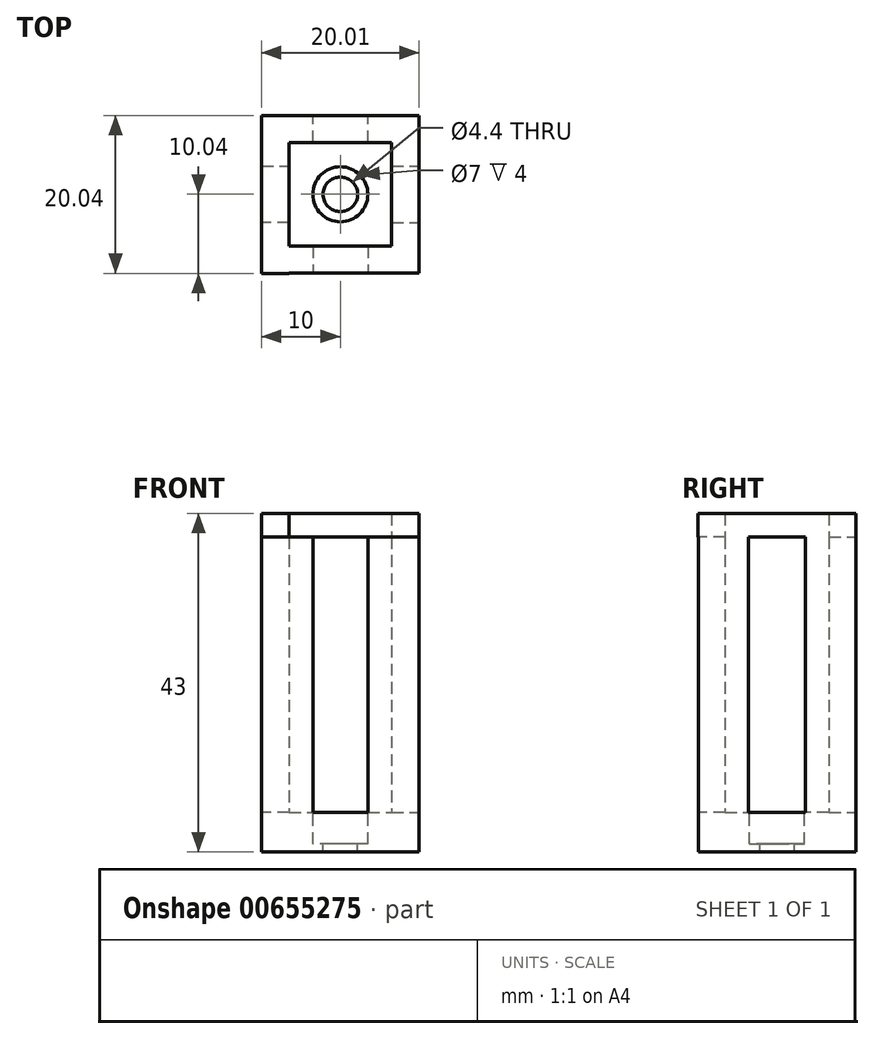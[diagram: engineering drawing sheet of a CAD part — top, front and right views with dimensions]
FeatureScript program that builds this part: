
annotation { "Feature Type Name" : "Feature", "Feature Type Description" : "" }
export const myFeature = defineFeature(function(context is Context, id is Id, definition is map)
    precondition{}
    {
        {
            var Q0;
            Q0=qCreatedBy(makeId("Top.planeOp"),FACE);
            var sketch = newSketch(context, id + "F0", { "sketchPlane" : qUnion([Q0])});
            skLineSegment(sketch, "E0.bottom", {"start": v(10, -10) * mm, "end": v(-10, -10) * mm});
            skLineSegment(sketch, "E0.top", {"start": v(10, 10) * mm, "end": v(-10, 10) * mm});
            skLineSegment(sketch, "E0.left", {"start": v(10, -10) * mm, "end": v(10, 10) * mm});
            skLineSegment(sketch, "E0.right", {"start": v(-10, -10) * mm, "end": v(-10, 10) * mm});
            skPoint(sketch, "E0.middle", {"position": v(0, 0) * mm});
            skSolve(sketch);
        }
        {
            var Q0;
            Q0=makeQuery(id+"F0.imprint","IMPRINT",FACE,{"disambiguationData":[TD([[makeQuery(id+"F0.imprint","IMPRINT",EDGE,{"derivedFrom":sQuery(id+"F0.wireOp",EDGE,"E0.bottom")}),-1.0]])]});
            extrude(context, id + "F1", {"entities" : qUnion([Q0]), "depth" : 5 * mm});
        }
        {
            var Q0;
            Q0=makeQuery(id+"F1.opExtrude","CAP_FACE",FACE,{"disambiguationData":[OSD([sQuery(id+"F0.wireOp",EDGE,"E0.bottom"),sQuery(id+"F0.wireOp",EDGE,"E0.top"),sQuery(id+"F0.wireOp",EDGE,"E0.left"),sQuery(id+"F0.wireOp",EDGE,"E0.right")])],"isStart":false});
            var sketch = newSketch(context, id + "F2", { "sketchPlane" : qUnion([Q0])});
            skPoint(sketch, "E1", {"position": v(0, 0) * mm});
            skSolve(sketch);
        }
        {
            var Q0;
            Q0=sQuery(id+"F2.wireOp",VERTEX,"E1");
            var Q1;
            Q1=makeQuery(id+"F1.opExtrude","SWEPT_BODY",BODY,{"disambiguationData":[OSD([sQuery(id+"F0.wireOp",EDGE,"E0.bottom"),sQuery(id+"F0.wireOp",EDGE,"E0.top"),sQuery(id+"F0.wireOp",EDGE,"E0.left"),sQuery(id+"F0.wireOp",EDGE,"E0.right")])]});
            hole(context, id + "F3", {"style" : HoleStyle.SIMPLE, "endStyle" : HoleEndStyle.THROUGH, "standardTappedOrClearance" : lookupTablePath({ "standard" : "ISO", "fit" : "Normal", "size" : "M4", "type" : "Clearance" }), "standardBlindInLast" : lookupTablePath({ "fit" : "Standard", "standard" : "ISO", "size" : "M4", "type" : "Clearance" }), "holeDiameter" : 4.4 * mm, "tappedDepth" : 12 * mm, "tapClearance" : 3, "locations" : qUnion([Q0]), "scope" : qUnion([Q1])});
        }
        {
            var Q0;
            Q0=makeQuery(id+"F1.opExtrude","CAP_FACE",FACE,{"disambiguationData":[OSD([sQuery(id+"F0.wireOp",EDGE,"E0.bottom"),sQuery(id+"F0.wireOp",EDGE,"E0.top"),sQuery(id+"F0.wireOp",EDGE,"E0.left"),sQuery(id+"F0.wireOp",EDGE,"E0.right")])],"isStart":false});
            var sketch = newSketch(context, id + "F4", { "sketchPlane" : qUnion([Q0])});
            skPoint(sketch, "E2.middle", {"position": v(0, 0) * mm});
            skLineSegment(sketch, "E3.bottom", {"start": v(-6.5, 6.6) * mm, "end": v(-10, 6.6) * mm});
            skLineSegment(sketch, "E3.top", {"start": v(-6.5, 10) * mm, "end": v(-10, 10) * mm});
            skLineSegment(sketch, "E3.left", {"start": v(-6.5, 6.6) * mm, "end": v(-6.5, 10) * mm});
            skLineSegment(sketch, "E3.right", {"start": v(-10, 6.6) * mm, "end": v(-10, 10) * mm});
            skLineSegment(sketch, "E4.bottom", {"start": v(6.5, 6.6) * mm, "end": v(10, 6.6) * mm});
            skLineSegment(sketch, "E4.top", {"start": v(6.5, 10) * mm, "end": v(10, 10) * mm});
            skLineSegment(sketch, "E4.left", {"start": v(6.5, 6.6) * mm, "end": v(6.5, 10) * mm});
            skLineSegment(sketch, "E4.right", {"start": v(10, 6.6) * mm, "end": v(10, 10) * mm});
            skLineSegment(sketch, "E5.bottom", {"start": v(6.5, -6.6) * mm, "end": v(10, -6.6) * mm});
            skLineSegment(sketch, "E5.top", {"start": v(6.5, -10) * mm, "end": v(10, -10) * mm});
            skLineSegment(sketch, "E5.left", {"start": v(6.5, -6.6) * mm, "end": v(6.5, -10) * mm});
            skLineSegment(sketch, "E5.right", {"start": v(10, -6.6) * mm, "end": v(10, -10) * mm});
            skLineSegment(sketch, "E6.bottom", {"start": v(-6.5, -6.6) * mm, "end": v(-10, -6.6) * mm});
            skLineSegment(sketch, "E6.top", {"start": v(-6.5, -10) * mm, "end": v(-10, -10) * mm});
            skLineSegment(sketch, "E6.left", {"start": v(-6.5, -6.6) * mm, "end": v(-6.5, -10) * mm});
            skLineSegment(sketch, "E6.right", {"start": v(-10, -6.6) * mm, "end": v(-10, -10) * mm});
            skLineSegment(sketch, "E7.bottom", {"start": v(-10, 6.6) * mm, "end": v(-6.5, 6.6) * mm});
            skLineSegment(sketch, "E7.top", {"start": v(-10, 3.6) * mm, "end": v(-6.5, 3.6) * mm});
            skLineSegment(sketch, "E7.left", {"start": v(-10, 6.6) * mm, "end": v(-10, 3.6) * mm});
            skLineSegment(sketch, "E7.right", {"start": v(-6.5, 6.6) * mm, "end": v(-6.5, 3.6) * mm});
            skLineSegment(sketch, "E8.top", {"start": v(-6.5, -3.6) * mm, "end": v(-10, -3.6) * mm});
            skLineSegment(sketch, "E8.left", {"start": v(-6.5, -6.6) * mm, "end": v(-6.5, -3.6) * mm});
            skLineSegment(sketch, "E8.right", {"start": v(-10, -6.6) * mm, "end": v(-10, -3.6) * mm});
            skLineSegment(sketch, "E9.bottom", {"start": v(-6.5, -6.6) * mm, "end": v(-3.5, -6.6) * mm});
            skLineSegment(sketch, "E9.top", {"start": v(-6.5, -10) * mm, "end": v(-3.5, -10) * mm});
            skLineSegment(sketch, "E9.right", {"start": v(-3.5, -6.6) * mm, "end": v(-3.5, -10) * mm});
            skLineSegment(sketch, "E10.bottom", {"start": v(3.5, -6.6) * mm, "end": v(6.5, -6.6) * mm});
            skLineSegment(sketch, "E10.top", {"start": v(3.5, -10) * mm, "end": v(6.5, -10) * mm});
            skLineSegment(sketch, "E10.left", {"start": v(3.5, -6.6) * mm, "end": v(3.5, -10) * mm});
            skLineSegment(sketch, "E11.top", {"start": v(6.5, -3.6) * mm, "end": v(10, -3.6) * mm});
            skLineSegment(sketch, "E11.left", {"start": v(6.5, -6.6) * mm, "end": v(6.5, -3.6) * mm});
            skLineSegment(sketch, "E11.right", {"start": v(10, -6.6) * mm, "end": v(10, -3.6) * mm});
            skLineSegment(sketch, "E12.top", {"start": v(6.5, 3.6) * mm, "end": v(10, 3.6) * mm});
            skLineSegment(sketch, "E12.left", {"start": v(6.5, 6.6) * mm, "end": v(6.5, 3.6) * mm});
            skLineSegment(sketch, "E12.right", {"start": v(10, 6.6) * mm, "end": v(10, 3.6) * mm});
            skLineSegment(sketch, "E13.bottom", {"start": v(6.5, 6.6) * mm, "end": v(3.5, 6.6) * mm});
            skLineSegment(sketch, "E13.top", {"start": v(6.5, 10) * mm, "end": v(3.5, 10) * mm});
            skLineSegment(sketch, "E13.right", {"start": v(3.5, 6.6) * mm, "end": v(3.5, 10) * mm});
            skLineSegment(sketch, "E14.bottom", {"start": v(-6.5, 6.6) * mm, "end": v(-3.5, 6.6) * mm});
            skLineSegment(sketch, "E14.top", {"start": v(-6.5, 10) * mm, "end": v(-3.5, 10) * mm});
            skLineSegment(sketch, "E14.right", {"start": v(-3.5, 6.6) * mm, "end": v(-3.5, 10) * mm});
            skSolve(sketch);
        }
        {
            var Q0;
            Q0=qSketchRegion(id+"F4",true);
            extrude(context, id + "F5", {"entities" : qUnion([Q0]), "operationType" : NewBodyOperationType.ADD, "depth" : 35 * mm});
        }
        {
            var Q0;
            Q0=makeQuery(id+"F5.opExtrude","CAP_FACE",FACE,{"disambiguationData":[OSD([sQuery(id+"F4.wireOp",EDGE,"E3.top"),sQuery(id+"F4.wireOp",EDGE,"E3.right"),sQuery(id+"F4.wireOp",EDGE,"E7.top"),sQuery(id+"F4.wireOp",EDGE,"E7.left"),sQuery(id+"F4.wireOp",EDGE,"E7.right"),sQuery(id+"F4.wireOp",EDGE,"E14.bottom"),sQuery(id+"F4.wireOp",EDGE,"E14.top"),sQuery(id+"F4.wireOp",EDGE,"E14.right")])],"isStart":false});
            var sketch = newSketch(context, id + "F6", { "sketchPlane" : qUnion([Q0])});
            skLineSegment(sketch, "E15", {"start": v(-6.17, 6.27) * mm, "end": v(-6.2, 6.27) * mm});
            skLineSegment(sketch, "E16", {"start": v(-6.18, 12.5) * mm, "end": v(-6.2, 12.5) * mm});
            skLineSegment(sketch, "E17.bottom", {"start": v(-10, 10) * mm, "end": v(-6.5, 10) * mm});
            skLineSegment(sketch, "E17.top", {"start": v(-10, -10.04) * mm, "end": v(-6.5, -10.04) * mm});
            skLineSegment(sketch, "E17.left", {"start": v(-10, 10) * mm, "end": v(-10, -10.04) * mm});
            skLineSegment(sketch, "E17.right", {"start": v(-6.5, 10) * mm, "end": v(-6.5, -10.04) * mm});
            skLineSegment(sketch, "E18.bottom", {"start": v(10, 10) * mm, "end": v(6.5, 10) * mm});
            skLineSegment(sketch, "E18.top", {"start": v(10, 1.06) * mm, "end": v(6.5, 1.06) * mm});
            skLineSegment(sketch, "E18.left", {"start": v(10, 10) * mm, "end": v(10, 1.06) * mm});
            skLineSegment(sketch, "E18.right", {"start": v(6.5, 10) * mm, "end": v(6.5, 1.06) * mm});
            skLineSegment(sketch, "E19.bottom", {"start": v(6.5, 1.06) * mm, "end": v(10, 1.06) * mm});
            skLineSegment(sketch, "E19.top", {"start": v(6.5, -10.01) * mm, "end": v(10, -10.01) * mm});
            skLineSegment(sketch, "E19.left", {"start": v(6.5, 1.06) * mm, "end": v(6.5, -10.01) * mm});
            skLineSegment(sketch, "E19.right", {"start": v(10, 1.06) * mm, "end": v(10, -10.01) * mm});
            skLineSegment(sketch, "E20.bottom", {"start": v(6.5, -10.01) * mm, "end": v(-6.5, -10.01) * mm});
            skLineSegment(sketch, "E20.top", {"start": v(6.5, -6.6) * mm, "end": v(-6.5, -6.6) * mm});
            skLineSegment(sketch, "E20.left", {"start": v(6.5, -10.01) * mm, "end": v(6.5, -6.6) * mm});
            skLineSegment(sketch, "E20.right", {"start": v(-6.5, -10.01) * mm, "end": v(-6.5, -6.6) * mm});
            skLineSegment(sketch, "E21.bottom", {"start": v(-6.5, 6.6) * mm, "end": v(6.5, 6.6) * mm});
            skLineSegment(sketch, "E21.top", {"start": v(-6.5, 10) * mm, "end": v(6.5, 10) * mm});
            skLineSegment(sketch, "E21.left", {"start": v(-6.5, 6.6) * mm, "end": v(-6.5, 10) * mm});
            skLineSegment(sketch, "E21.right", {"start": v(6.5, 6.6) * mm, "end": v(6.5, 10) * mm});
            skSolve(sketch);
        }
        {
            var Q0;
            Q0=qSketchRegion(id+"F6",true);
            extrude(context, id + "F7", {"entities" : qUnion([Q0]), "operationType" : NewBodyOperationType.ADD, "depth" : 1 * mm});
        }
        {
            var Q0;
            Q0=makeQuery(id+"F1.opExtrude","CAP_FACE",FACE,{"disambiguationData":[OSD([sQuery(id+"F0.wireOp",EDGE,"E0.bottom"),sQuery(id+"F0.wireOp",EDGE,"E0.top"),sQuery(id+"F0.wireOp",EDGE,"E0.left"),sQuery(id+"F0.wireOp",EDGE,"E0.right")])],"isStart":false});
            var sketch = newSketch(context, id + "F8", { "sketchPlane" : qUnion([Q0])});
            skPoint(sketch, "E22", {"position": v(0, 0) * mm});
            skSolve(sketch);
        }
        {
            var Q0;
            Q0=makeQuery(id+"F8.imprint","IMPRINT",FACE,{"disambiguationData":[TD([[makeQuery(id+"F8.imprint","IMPRINT",EDGE,{"derivedFrom":makeQuery(id+"F1.opExtrude","CAP_EDGE",EDGE,{"disambiguationData":[OSD([sQuery(id+"F0.wireOp",EDGE,"E0.bottom")])],"isStart":false})}),-1.0]])]});
            var sketch = newSketch(context, id + "F9", { "sketchPlane" : qUnion([Q0])});
            skCircle(sketch, "E23", {"center": v(0, 0) * mm, "radius": 3.5 * mm});
            skSolve(sketch);
        }
        {
            var Q0;
            Q0=qSketchRegion(id+"F9",true);
            extrude(context, id + "F10", {"entities" : qUnion([Q0]), "operationType" : NewBodyOperationType.REMOVE, "oppositeDirection" : true, "depth" : 4 * mm});
        }
        {
            var Q0;
            Q0=makeQuery(id+"F7.opExtrude","CAP_FACE",FACE,{"disambiguationData":[OSD([sQuery(id+"F6.wireOp",EDGE,"E17.bottom"),sQuery(id+"F6.wireOp",EDGE,"E17.top"),sQuery(id+"F6.wireOp",EDGE,"E17.left"),sQuery(id+"F6.wireOp",EDGE,"E17.right"),sQuery(id+"F6.wireOp",EDGE,"E18.bottom"),sQuery(id+"F6.wireOp",EDGE,"E18.left"),sQuery(id+"F6.wireOp",EDGE,"E18.right"),sQuery(id+"F6.wireOp",EDGE,"E19.top"),sQuery(id+"F6.wireOp",EDGE,"E19.left"),sQuery(id+"F6.wireOp",EDGE,"E19.right"),sQuery(id+"F6.wireOp",EDGE,"E20.bottom"),sQuery(id+"F6.wireOp",EDGE,"E20.top"),sQuery(id+"F6.wireOp",EDGE,"E21.bottom"),sQuery(id+"F6.wireOp",EDGE,"E21.top")])],"isStart":false});
            extrude(context, id + "F11", {"entities" : qUnion([Q0]), "operationType" : NewBodyOperationType.ADD, "depth" : 2 * mm});
        }
    });
